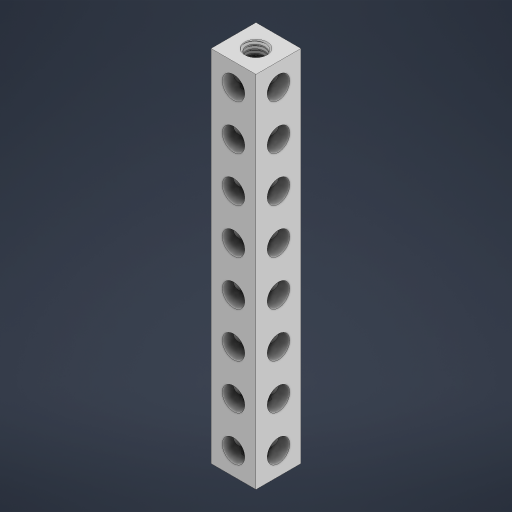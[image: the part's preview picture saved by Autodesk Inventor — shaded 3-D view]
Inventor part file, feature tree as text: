
AUTODESK INVENTOR PART (.ipt)
format: ipt  version: 2023 (Build 270158000, 158)  size: 1,332,736 bytes
history: native  units: in
note: dims shown in document units (in); Inventor stores cm internally (conversion verified against a paired STEP export)
features: mirror x1
ambient origin geometry x8: Origin, YZ Plane, XZ Plane, XY Plane, X Axis, Y Axis, Z Axis, Center Point
bodies: Solid1 (feature_tree)
feature tree (1):
  mirror  "Mirror3"
